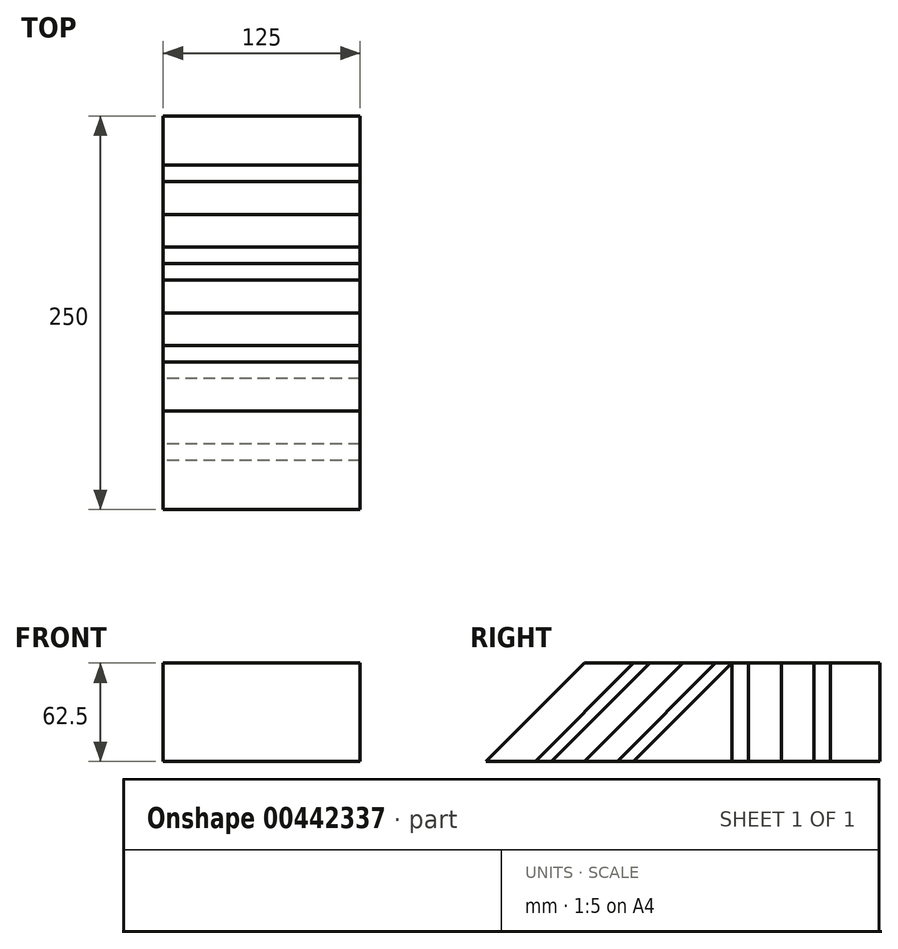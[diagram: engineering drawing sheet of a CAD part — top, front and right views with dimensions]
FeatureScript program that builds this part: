
annotation { "Feature Type Name" : "Feature", "Feature Type Description" : "" }
export const myFeature = defineFeature(function(context is Context, id is Id, definition is map)
    precondition{}
    {
        {
            var Q0;
            Q0=qCreatedBy(makeId("Front.planeOp"),FACE);
            var sketch = newSketch(context, id + "F0", { "sketchPlane" : qUnion([Q0])});
            skLineSegment(sketch, "E0.bottom", {"start": v(62.5, 31.25) * mm, "end": v(-62.5, 31.25) * mm});
            skLineSegment(sketch, "E0.top", {"start": v(62.5, -31.25) * mm, "end": v(-62.5, -31.25) * mm});
            skLineSegment(sketch, "E0.left", {"start": v(62.5, 31.25) * mm, "end": v(62.5, -31.25) * mm});
            skLineSegment(sketch, "E0.right", {"start": v(-62.5, 31.25) * mm, "end": v(-62.5, -31.25) * mm});
            skPoint(sketch, "E0.middle", {"position": v(0, 0) * mm});
            skSolve(sketch);
        }
        {
            var Q0;
            Q0=makeQuery(id+"F0.imprint","IMPRINT",FACE,{"disambiguationData":[TD([[makeQuery(id+"F0.imprint","IMPRINT",EDGE,{"derivedFrom":sQuery(id+"F0.wireOp",EDGE,"E0.bottom")}),1.0]])]});
            extrude(context, id + "F1", {"entities" : qUnion([Q0]), "endBound" : BoundingType.SYMMETRIC, "depth" : 250 * mm});
        }
        {
            var Q0;
            Q0 = qSketchRegion(id + "F0", true);
            extrude(context, id + "F2", {"entities" : qUnion([Q0]), "endBound" : BoundingType.SYMMETRIC, "depth" : 125 * mm});
        }
        {
            var Q0;
            Q0=makeQuery(id+"F0.imprint","IMPRINT",FACE,{"disambiguationData":[TD([[makeQuery(id+"F0.imprint","IMPRINT",EDGE,{"derivedFrom":sQuery(id+"F0.wireOp",EDGE,"E0.bottom")}),1.0]])]});
            extrude(context, id + "F3", {"entities" : qUnion([Q0]), "endBound" : BoundingType.SYMMETRIC, "depth" : (250 * 3 / 4) * mm});
        }
        {
            var Q0;
            Q0=makeQuery(id+"F0.imprint","IMPRINT",FACE,{"disambiguationData":[TD([[makeQuery(id+"F0.imprint","IMPRINT",EDGE,{"derivedFrom":sQuery(id+"F0.wireOp",EDGE,"E0.bottom")}),1.0]])]});
            extrude(context, id + "F4", {"entities" : qUnion([Q0]), "endBound" : BoundingType.SYMMETRIC, "depth" : (250 / 4) * mm});
        }
        {
            var Q0;
            Q0=makeQuery(id+"F0.imprint","IMPRINT",FACE,{"disambiguationData":[TD([[makeQuery(id+"F0.imprint","IMPRINT",EDGE,{"derivedFrom":sQuery(id+"F0.wireOp",EDGE,"E0.bottom")}),1.0]])]});
            extrude(context, id + "F5", {"entities" : qUnion([Q0]), "endBound" : BoundingType.SYMMETRIC, "depth" : 250 * 2 / 3 * mm});
        }
        {
            var Q0;
            Q0=makeQuery(id+"F0.imprint","IMPRINT",FACE,{"disambiguationData":[TD([[makeQuery(id+"F0.imprint","IMPRINT",EDGE,{"derivedFrom":sQuery(id+"F0.wireOp",EDGE,"E0.bottom")}),1.0]])]});
            extrude(context, id + "F6", {"entities" : qUnion([Q0]), "endBound" : BoundingType.SYMMETRIC, "depth" : (250 / 3) * mm});
        }
        {
            var Q0;
            Q0=makeQuery(id+"F1.opExtrude","CAP_EDGE",EDGE,{"disambiguationData":[OSD([sQuery(id+"F0.wireOp",EDGE,"E0.bottom")])],"isStart":false});
            chamfer(context, id + "F7", {"entities" : qUnion([Q0]), "chamferType" : ChamferType.TWO_OFFSETS, "width1" : 62.5 * mm, "oppositeDirection" : false, "width2" : 62.5 * mm, "tangentPropagation" : true});
        }
        {
            var Q0;
            Q0=makeQuery(id+"F2.opExtrude","CAP_EDGE",EDGE,{"disambiguationData":[OSD([sQuery(id+"F0.wireOp",EDGE,"E0.bottom")])],"isStart":false});
            chamfer(context, id + "F8", {"entities" : qUnion([Q0]), "width" : 62.5 * mm, "tangentPropagation" : true});
        }
        {
            var Q0;
            Q0=makeQuery(id+"F3.opExtrude","CAP_EDGE",EDGE,{"disambiguationData":[OSD([sQuery(id+"F0.wireOp",EDGE,"E0.bottom")])],"isStart":false});
            chamfer(context, id + "F9", {"entities" : qUnion([Q0]), "width" : 62.5 * mm, "tangentPropagation" : true});
        }
        {
            var Q0;
            Q0=makeQuery(id+"F5.opExtrude","CAP_EDGE",EDGE,{"disambiguationData":[OSD([sQuery(id+"F0.wireOp",EDGE,"E0.bottom")])],"isStart":false});
            chamfer(context, id + "F10", {"entities" : qUnion([Q0]), "width" : 62.5 * mm, "tangentPropagation" : true});
        }
        {
            var Q0;
            Q0=makeQuery(id+"F4.opExtrude","CAP_EDGE",EDGE,{"disambiguationData":[OSD([sQuery(id+"F0.wireOp",EDGE,"E0.bottom")])],"isStart":false});
            chamfer(context, id + "F11", {"entities" : qUnion([Q0]), "width" : 62.5 * mm, "tangentPropagation" : true});
        }
        {
            var Q0;
            Q0=makeQuery(id+"F6.opExtrude","CAP_EDGE",EDGE,{"disambiguationData":[OSD([sQuery(id+"F0.wireOp",EDGE,"E0.bottom")])],"isStart":false});
            chamfer(context, id + "F12", {"entities" : qUnion([Q0]), "width" : 62.5 * mm, "tangentPropagation" : true});
        }
    });
